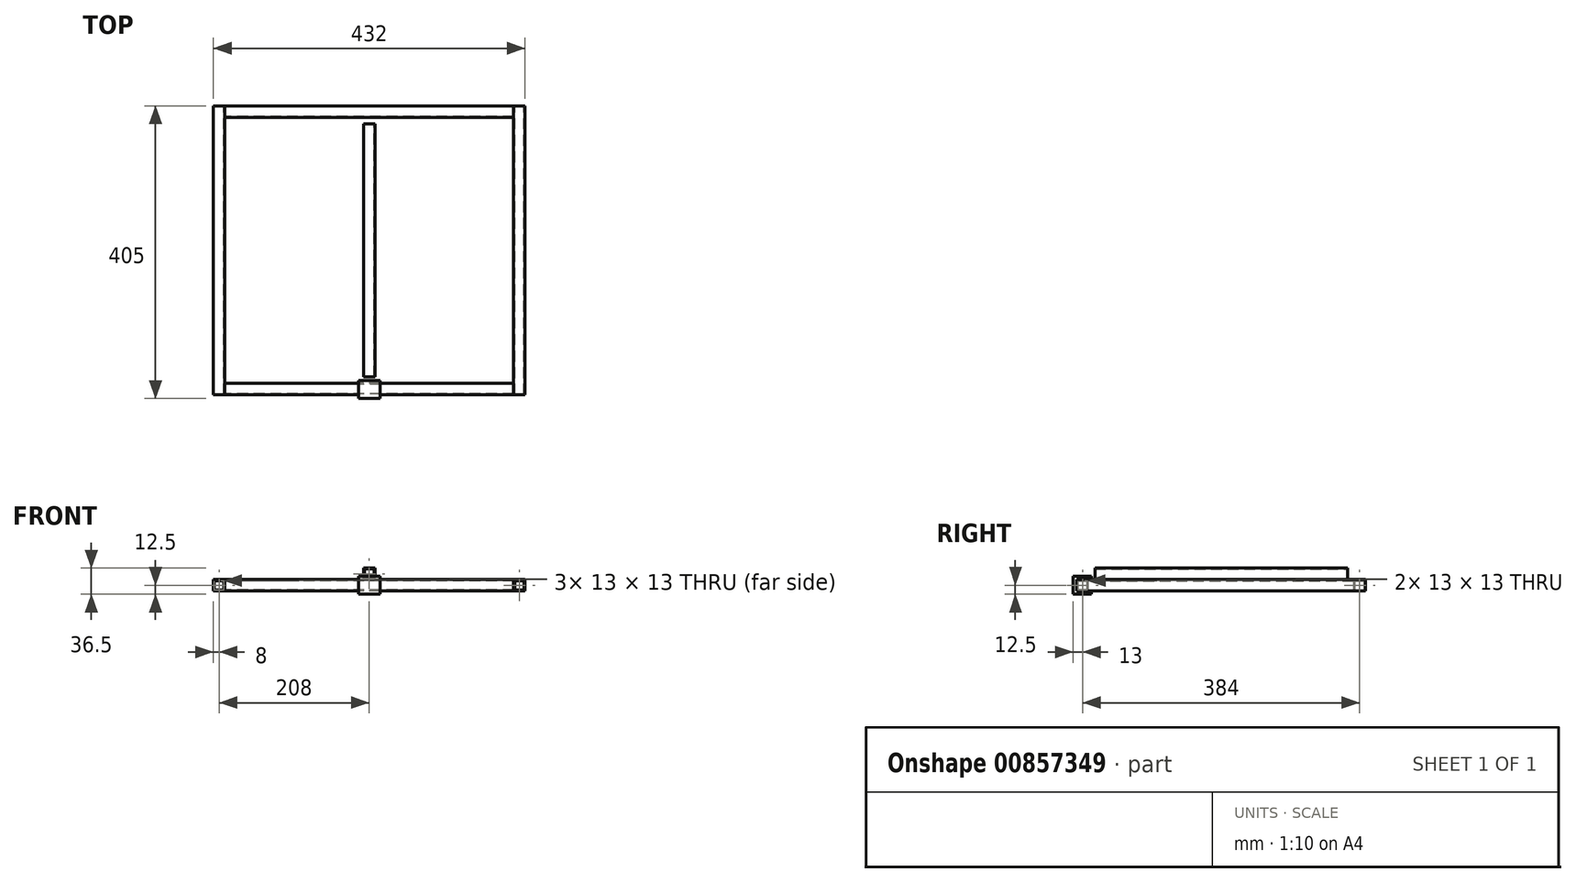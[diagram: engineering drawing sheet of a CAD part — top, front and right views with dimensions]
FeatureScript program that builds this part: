
annotation { "Feature Type Name" : "Feature", "Feature Type Description" : "" }
export const myFeature = defineFeature(function(context is Context, id is Id, definition is map)
    precondition{}
    {
        {
            var Q0;
            Q0=qCreatedBy(makeId("Front.planeOp"),FACE);
            var sketch = newSketch(context, id + "F0", { "sketchPlane" : qUnion([Q0])});
            skLineSegment(sketch, "E0.bottom", {"start": v(-200, -8) * mm, "end": v(-216, -8) * mm});
            skLineSegment(sketch, "E0.top", {"start": v(-200, 8) * mm, "end": v(-216, 8) * mm});
            skLineSegment(sketch, "E0.left", {"start": v(-200, -8) * mm, "end": v(-200, 8) * mm});
            skLineSegment(sketch, "E0.right", {"start": v(-216, -8) * mm, "end": v(-216, 8) * mm});
            skPoint(sketch, "E0.middle", {"position": v(-208, 0) * mm});
            skLineSegment(sketch, "E1.0", {"start": v(-201.5, 6.5) * mm, "end": v(-214.5, 6.5) * mm});
            skLineSegment(sketch, "E1.1", {"start": v(-201.5, -6.5) * mm, "end": v(-201.5, 6.5) * mm});
            skLineSegment(sketch, "E1.2", {"start": v(-201.5, -6.5) * mm, "end": v(-214.5, -6.5) * mm});
            skLineSegment(sketch, "E1.3", {"start": v(-214.5, -6.5) * mm, "end": v(-214.5, 6.5) * mm});
            skLineSegment(sketch, "E2.MirrorCS", {"start": v(201.5, -6.5) * mm, "end": v(214.5, -6.5) * mm});
            skLineSegment(sketch, "E3.MirrorCS", {"start": v(201.5, 6.5) * mm, "end": v(214.5, 6.5) * mm});
            skLineSegment(sketch, "E4.MirrorCS", {"start": v(200, -8) * mm, "end": v(216, -8) * mm});
            skLineSegment(sketch, "E5.MirrorCS", {"start": v(216, -8) * mm, "end": v(216, 8) * mm});
            skLineSegment(sketch, "E6.MirrorCS", {"start": v(214.5, -6.5) * mm, "end": v(214.5, 6.5) * mm});
            skLineSegment(sketch, "E7.MirrorCS", {"start": v(200, 8) * mm, "end": v(216, 8) * mm});
            skLineSegment(sketch, "E8.MirrorCS", {"start": v(201.5, -6.5) * mm, "end": v(201.5, 6.5) * mm});
            skLineSegment(sketch, "E9.MirrorCS", {"start": v(200, -8) * mm, "end": v(200, 8) * mm});
            skPoint(sketch, "E10.MirrorP", {"position": v(208, 0) * mm});
            skSolve(sketch);
        }
        {
            var Q0;
            Q0=makeQuery(id+"F0.imprint","IMPRINT",FACE,{"disambiguationData":[TD([[makeQuery(id+"F0.imprint","IMPRINT",EDGE,{"derivedFrom":sQuery(id+"F0.wireOp",EDGE,"E0.bottom")}),-1.0]])]});
            var Q1;
            Q1=makeQuery(id+"F0.imprint","IMPRINT",FACE,{"disambiguationData":[TD([[makeQuery(id+"F0.imprint","IMPRINT",EDGE,{"derivedFrom":sQuery(id+"F0.wireOp",EDGE,"E2.MirrorCS")}),-1.0]])]});
            extrude(context, id + "F1", {"entities" : qUnion([Q0, Q1]), "endBound" : BoundingType.SYMMETRIC, "depth" : 400 * mm, "offsetDistance" : 25 * mm});
        }
        {
            var Q0;
            Q0=qCreatedBy(makeId("Right.planeOp"),FACE);
            var sketch = newSketch(context, id + "F2", { "sketchPlane" : qUnion([Q0])});
            skPoint(sketch, "E11.0", {"position": v(-200, 8) * mm});
            skPoint(sketch, "E12.0", {"position": v(-200, -8) * mm});
            skLineSegment(sketch, "E13.bottom", {"start": v(-200, 8) * mm, "end": v(-184, 8) * mm});
            skLineSegment(sketch, "E13.top", {"start": v(-200, -8) * mm, "end": v(-184, -8) * mm});
            skLineSegment(sketch, "E13.left", {"start": v(-200, 8) * mm, "end": v(-200, -8) * mm});
            skLineSegment(sketch, "E13.right", {"start": v(-184, 8) * mm, "end": v(-184, -8) * mm});
            skLineSegment(sketch, "E14.0", {"start": v(-198.5, 6.5) * mm, "end": v(-185.5, 6.5) * mm});
            skLineSegment(sketch, "E14.1", {"start": v(-198.5, 6.5) * mm, "end": v(-198.5, -6.5) * mm});
            skLineSegment(sketch, "E14.2", {"start": v(-198.5, -6.5) * mm, "end": v(-185.5, -6.5) * mm});
            skLineSegment(sketch, "E14.3", {"start": v(-185.5, 6.5) * mm, "end": v(-185.5, -6.5) * mm});
            skPoint(sketch, "E15.MirrorP", {"position": v(200, -8) * mm});
            skLineSegment(sketch, "E16.MirrorCS", {"start": v(200, -8) * mm, "end": v(184, -8) * mm});
            skLineSegment(sketch, "E17.MirrorCS", {"start": v(198.5, 6.5) * mm, "end": v(185.5, 6.5) * mm});
            skLineSegment(sketch, "E18.MirrorCS", {"start": v(200, 8) * mm, "end": v(200, -8) * mm});
            skLineSegment(sketch, "E19.MirrorCS", {"start": v(184, 8) * mm, "end": v(184, -8) * mm});
            skLineSegment(sketch, "E20.MirrorCS", {"start": v(185.5, 6.5) * mm, "end": v(185.5, -6.5) * mm});
            skPoint(sketch, "E21.MirrorP", {"position": v(200, 8) * mm});
            skLineSegment(sketch, "E22.MirrorCS", {"start": v(198.5, -6.5) * mm, "end": v(185.5, -6.5) * mm});
            skLineSegment(sketch, "E23.MirrorCS", {"start": v(198.5, 6.5) * mm, "end": v(198.5, -6.5) * mm});
            skLineSegment(sketch, "E24.MirrorCS", {"start": v(200, 8) * mm, "end": v(184, 8) * mm});
            skSolve(sketch);
        }
        {
            var Q0;
            Q0=makeQuery(id+"F2.imprint","IMPRINT",FACE,{"disambiguationData":[TD([[makeQuery(id+"F2.imprint","IMPRINT",EDGE,{"derivedFrom":sQuery(id+"F2.wireOp",EDGE,"E13.bottom")}),-1.0]])]});
            var Q1;
            Q1=makeQuery(id+"F2.imprint","IMPRINT",FACE,{"disambiguationData":[TD([[makeQuery(id+"F2.imprint","IMPRINT",EDGE,{"derivedFrom":sQuery(id+"F2.wireOp",EDGE,"E16.MirrorCS")}),-1.0]])]});
            extrude(context, id + "F3", {"entities" : qUnion([Q0, Q1]), "endBound" : BoundingType.UP_TO_NEXT, "depth" : 25 * mm, "offsetDistance" : 25 * mm, "hasSecondDirection" : true, "secondDirectionBound" : SecondDirectionBoundingType.UP_TO_NEXT, "secondDirectionOppositeDirection" : true, "secondDirectionDepth" : 25 * mm});
        }
        {
            var Q0;
            Q0=makeQuery(id+"F1.opExtrude","SWEPT_FACE",FACE,{"disambiguationData":[OSD([sQuery(id+"F0.wireOp",EDGE,"E0.bottom")])]});
            var sketch = newSketch(context, id + "F4", { "sketchPlane" : qUnion([Q0])});
            skPoint(sketch, "E25.0", {"position": v(-200, 184) * mm});
            skPoint(sketch, "E26.0", {"position": v(200, 184) * mm});
            skPoint(sketch, "E27.0", {"position": v(200, -184) * mm});
            skPoint(sketch, "E28.0", {"position": v(-200, -184) * mm});
            skLineSegment(sketch, "E29.bottom", {"start": v(-216, 200) * mm, "end": v(-200, 200) * mm});
            skLineSegment(sketch, "E29.top", {"start": v(-216, 184) * mm, "end": v(-200, 184) * mm});
            skLineSegment(sketch, "E29.left", {"start": v(-216, 200) * mm, "end": v(-216, 184) * mm});
            skLineSegment(sketch, "E29.right", {"start": v(-200, 200) * mm, "end": v(-200, 184) * mm});
            skPoint(sketch, "E30.0", {"position": v(216, 200) * mm});
            skPoint(sketch, "E31.0", {"position": v(216, -200) * mm});
            skPoint(sketch, "E32.0", {"position": v(-216, -200) * mm});
            skLineSegment(sketch, "E33.bottom", {"start": v(216, 200) * mm, "end": v(200, 200) * mm});
            skLineSegment(sketch, "E33.top", {"start": v(216, 184) * mm, "end": v(200, 184) * mm});
            skLineSegment(sketch, "E33.left", {"start": v(216, 200) * mm, "end": v(216, 184) * mm});
            skLineSegment(sketch, "E33.right", {"start": v(200, 200) * mm, "end": v(200, 184) * mm});
            skLineSegment(sketch, "E34.bottom", {"start": v(216, -200) * mm, "end": v(200, -200) * mm});
            skLineSegment(sketch, "E34.top", {"start": v(216, -184) * mm, "end": v(200, -184) * mm});
            skLineSegment(sketch, "E34.left", {"start": v(216, -200) * mm, "end": v(216, -184) * mm});
            skLineSegment(sketch, "E34.right", {"start": v(200, -200) * mm, "end": v(200, -184) * mm});
            skLineSegment(sketch, "E35.bottom", {"start": v(-216, -200) * mm, "end": v(-200, -200) * mm});
            skLineSegment(sketch, "E35.top", {"start": v(-216, -184) * mm, "end": v(-200, -184) * mm});
            skLineSegment(sketch, "E35.left", {"start": v(-216, -200) * mm, "end": v(-216, -184) * mm});
            skLineSegment(sketch, "E35.right", {"start": v(-200, -200) * mm, "end": v(-200, -184) * mm});
            skLineSegment(sketch, "E36.0", {"start": v(-214.5, 198.5) * mm, "end": v(-201.5, 198.5) * mm});
            skLineSegment(sketch, "E36.1", {"start": v(-214.5, 198.5) * mm, "end": v(-214.5, 185.5) * mm});
            skLineSegment(sketch, "E36.2", {"start": v(-214.5, 185.5) * mm, "end": v(-201.5, 185.5) * mm});
            skLineSegment(sketch, "E36.3", {"start": v(-201.5, 198.5) * mm, "end": v(-201.5, 185.5) * mm});
            skLineSegment(sketch, "E37.0", {"start": v(214.5, 198.5) * mm, "end": v(201.5, 198.5) * mm});
            skLineSegment(sketch, "E37.1", {"start": v(214.5, 198.5) * mm, "end": v(214.5, 185.5) * mm});
            skLineSegment(sketch, "E37.2", {"start": v(214.5, 185.5) * mm, "end": v(201.5, 185.5) * mm});
            skLineSegment(sketch, "E37.3", {"start": v(201.5, 198.5) * mm, "end": v(201.5, 185.5) * mm});
            skLineSegment(sketch, "E38.0", {"start": v(214.5, -198.5) * mm, "end": v(201.5, -198.5) * mm});
            skLineSegment(sketch, "E38.1", {"start": v(214.5, -198.5) * mm, "end": v(214.5, -185.5) * mm});
            skLineSegment(sketch, "E38.2", {"start": v(214.5, -185.5) * mm, "end": v(201.5, -185.5) * mm});
            skLineSegment(sketch, "E38.3", {"start": v(201.5, -198.5) * mm, "end": v(201.5, -185.5) * mm});
            skLineSegment(sketch, "E39.0", {"start": v(-214.5, -198.5) * mm, "end": v(-201.5, -198.5) * mm});
            skLineSegment(sketch, "E39.1", {"start": v(-214.5, -198.5) * mm, "end": v(-214.5, -185.5) * mm});
            skLineSegment(sketch, "E39.2", {"start": v(-214.5, -185.5) * mm, "end": v(-201.5, -185.5) * mm});
            skLineSegment(sketch, "E39.3", {"start": v(-201.5, -198.5) * mm, "end": v(-201.5, -185.5) * mm});
            skSolve(sketch);
        }
        {
            var Q0;
            Q0=qCreatedBy(makeId("Front.planeOp"),FACE);
            var sketch = newSketch(context, id + "F5", { "sketchPlane" : qUnion([Q0])});
            skPoint(sketch, "E40.0", {"position": v(0, 8) * mm});
            skLineSegment(sketch, "E41.bottom", {"start": v(-8, 8) * mm, "end": v(8, 8) * mm});
            skLineSegment(sketch, "E41.top", {"start": v(-8, 24) * mm, "end": v(8, 24) * mm});
            skLineSegment(sketch, "E41.left", {"start": v(-8, 8) * mm, "end": v(-8, 24) * mm});
            skLineSegment(sketch, "E41.right", {"start": v(8, 8) * mm, "end": v(8, 24) * mm});
            skLineSegment(sketch, "E42.0", {"start": v(-6.5, 22.5) * mm, "end": v(6.5, 22.5) * mm});
            skLineSegment(sketch, "E42.1", {"start": v(-6.5, 9.5) * mm, "end": v(-6.5, 22.5) * mm});
            skLineSegment(sketch, "E42.2", {"start": v(-6.5, 9.5) * mm, "end": v(6.5, 9.5) * mm});
            skLineSegment(sketch, "E42.3", {"start": v(6.5, 9.5) * mm, "end": v(6.5, 22.5) * mm});
            skSolve(sketch);
        }
        {
            var Q0;
            Q0=makeQuery(id+"F5.imprint","IMPRINT",FACE,{"disambiguationData":[TD([[makeQuery(id+"F5.imprint","IMPRINT",EDGE,{"derivedFrom":sQuery(id+"F5.wireOp",EDGE,"E41.bottom")}),1.0]])]});
            extrude(context, id + "F6", {"entities" : qUnion([Q0]), "endBound" : BoundingType.SYMMETRIC, "depth" : 350 * mm, "offsetDistance" : 25 * mm});
        }
        {
            var Q0;
            Q0=makeQuery(id+"F3.opExtrude","SWEPT_FACE",FACE,{"disambiguationData":[OSD([sQuery(id+"F2.wireOp",EDGE,"E13.left")])]});
            var sketch = newSketch(context, id + "F7", { "sketchPlane" : qUnion([Q0])});
            skLineSegment(sketch, "E43.bottom", {"start": v(-15, 12.5) * mm, "end": v(15, 12.5) * mm});
            skLineSegment(sketch, "E43.top", {"start": v(-15, -12.5) * mm, "end": v(15, -12.5) * mm});
            skLineSegment(sketch, "E43.left", {"start": v(-15, 12.5) * mm, "end": v(-15, -12.5) * mm});
            skLineSegment(sketch, "E43.right", {"start": v(15, 12.5) * mm, "end": v(15, -12.5) * mm});
            skPoint(sketch, "E43.middle", {"position": v(0, 0) * mm});
            skSolve(sketch);
        }
        {
            var Q0;
            {var subQ0=sQuery(id+"F7.wireOp",EDGE,"E43.bottom");Q0=makeQuery(id+"F7.imprint","IMPRINT",FACE,{"disambiguationData":[TD([[makeQuery(id+"F7.imprint","IMPRINT",EDGE,{"derivedFrom":subQ0}),-1.0]])]});}
            var Q1;
            {var subQ0=sQuery(id+"F7.wireOp",EDGE,"E43.top");Q1=makeQuery(id+"F7.imprint","IMPRINT",FACE,{"disambiguationData":[TD([[makeQuery(id+"F7.imprint","IMPRINT",EDGE,{"derivedFrom":subQ0}),1.0]])]});}
            extrude(context, id + "F8", {"entities" : qUnion([Q0, Q1]), "oppositeDirection" : true, "depth" : 20 * mm, "offsetDistance" : 25 * mm});
        }
        {
            var Q0;
            {var subQ0=sQuery(id+"F7.wireOp",EDGE,"E43.left");var subQ1=makeQuery(id+"F3.opExtrude","SWEPT_EDGE",EDGE,{"disambiguationData":[OSD([sQuery(id+"F0.wireOp",EDGE,"E0.top"),sQuery(id+"F0.wireOp",EDGE,"E0.left")])]});var subQ2=makeQuery(id+"F7.imprint","INTERSECT",VERTEX,{"derivedFrom":[subQ1,subQ0]});Q0=makeQuery(id+"F7.imprint","IMPRINT",FACE,{"disambiguationData":[TD([[makeQuery(id+"F7.imprint","IMPRINT",EDGE,{"disambiguationData":[TD([[subQ2,-1.0]])],"derivedFrom":subQ0}),1.0]])]});}
            var Q1;
            {var subQ0=sQuery(id+"F7.wireOp",EDGE,"E43.bottom");Q1=makeQuery(id+"F7.imprint","IMPRINT",FACE,{"disambiguationData":[TD([[makeQuery(id+"F7.imprint","IMPRINT",EDGE,{"derivedFrom":subQ0}),-1.0]])]});}
            var Q2;
            {var subQ0=sQuery(id+"F7.wireOp",EDGE,"E43.top");Q2=makeQuery(id+"F7.imprint","IMPRINT",FACE,{"disambiguationData":[TD([[makeQuery(id+"F7.imprint","IMPRINT",EDGE,{"derivedFrom":subQ0}),1.0]])]});}
            extrude(context, id + "F9", {"entities" : qUnion([Q0, Q1, Q2]), "operationType" : NewBodyOperationType.ADD, "depth" : 5 * mm, "offsetDistance" : 25 * mm});
        }
    });
